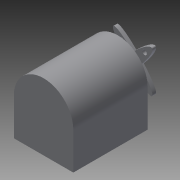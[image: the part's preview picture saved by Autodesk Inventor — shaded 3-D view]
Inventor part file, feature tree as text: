
AUTODESK INVENTOR PART (.ipt)
format: ipt  version: 2014 (Build 180170000, 170)  size: 144,384 bytes
history: native  units: mm
features: extrude x4, sketch x4
ambient origin geometry x8: Origin, YZ Plane, XZ Plane, XY Plane, X Axis, Y Axis, Z Axis, Center Point
bodies: Solid1 (feature_tree)
feature tree (8):
  extrude  "Extrusion1"  Depth=50.0mm TaperAngle=0.0deg
  extrude  "Extrusion2"  Depth=10.0mm TaperAngle=0.0deg
  extrude  "Extrusion3"  Depth=3.0mm
  extrude  "Extrusion4"  Depth=2.5mm
  sketch  "Sketch1"  dims[d0=40.0mm d2=50.0mm d3=0.0mm]
  sketch  "Sketch2"  dims[d4=7.5mm d5=10.0mm d6=0.0mm]
  sketch  "Sketch3"  dims[d7=3.0mm d8=3.0mm]
  sketch  "Sketch4"  dims[d9=3.0mm d10=3.0mm d11=2.5mm d12=0.0mm d13=2.5mm d14=0.0mm]
